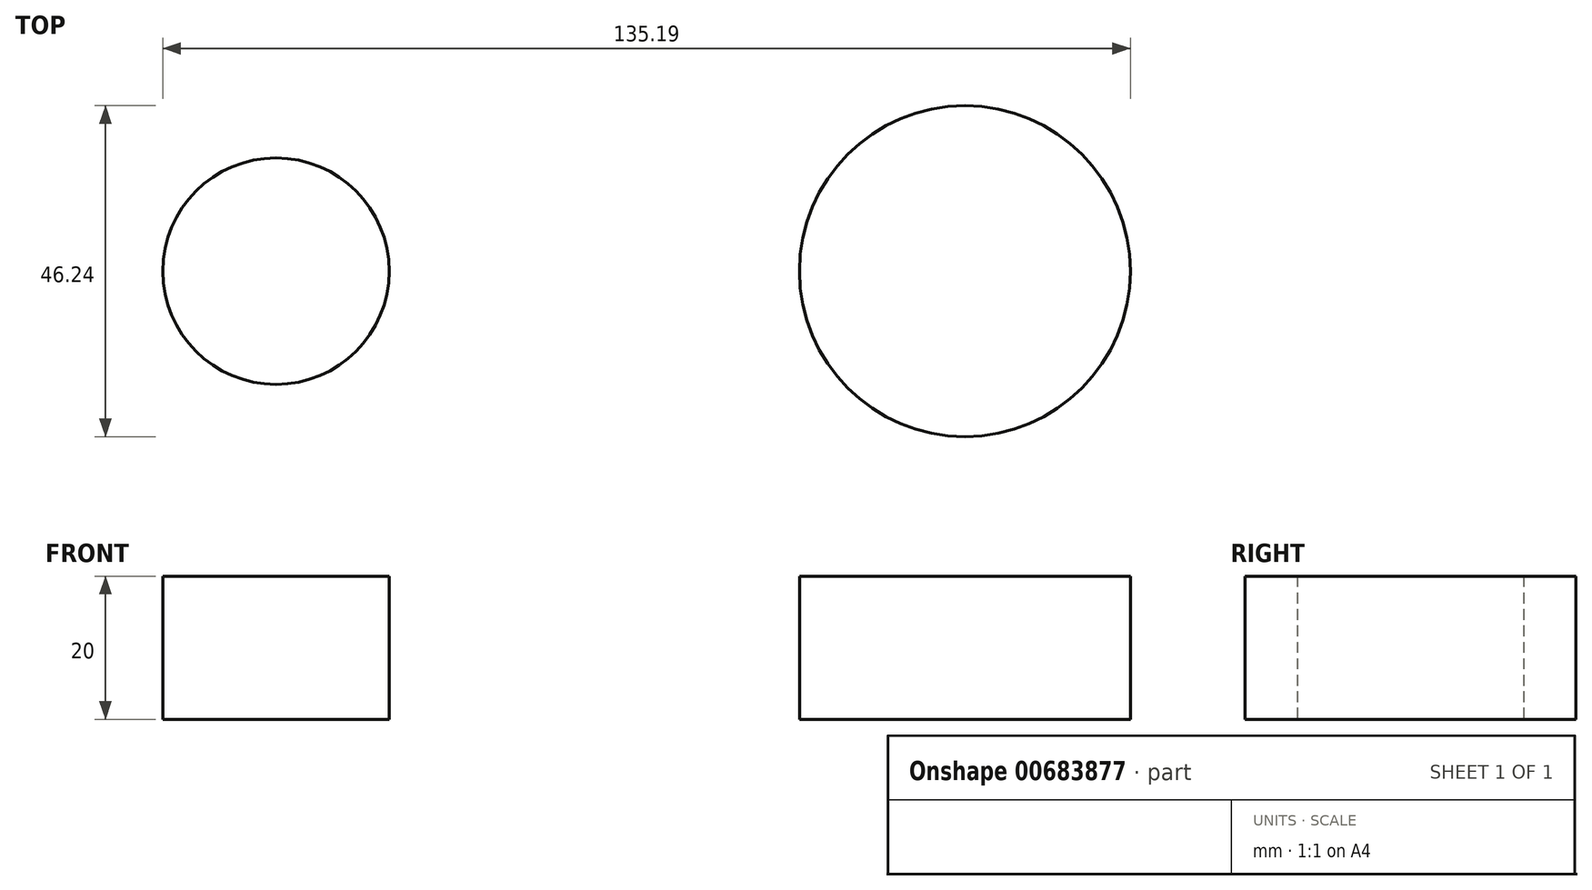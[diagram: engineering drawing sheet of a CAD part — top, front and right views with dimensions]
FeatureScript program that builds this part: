
annotation { "Feature Type Name" : "Feature", "Feature Type Description" : "" }
export const myFeature = defineFeature(function(context is Context, id is Id, definition is map)
    precondition{}
    {
        {
            var Q0;
            Q0=qCreatedBy(makeId("Top.planeOp"),FACE);
            var sketch = newSketch(context, id + "F0", { "sketchPlane" : qUnion([Q0])});
            skCircle(sketch, "E0", {"center": v(46.56, 0) * mm, "radius": 23.12 * mm});
            skSolve(sketch);
        }
        {
            var Q0;
            Q0=makeQuery(id+"F0.imprint","IMPRINT",FACE,{"disambiguationData":[TD([[makeQuery(id+"F0.imprint","IMPRINT",EDGE,{"derivedFrom":sQuery(id+"F0.wireOp",EDGE,"E0")}),1.0]])]});
            extrude(context, id + "F1", {"entities" : qUnion([Q0]), "depth" : 20 * mm, "offsetDistance" : 25 * mm});
        }
        {
            var Q0;
            Q0=qCreatedBy(makeId("Top.planeOp"),FACE);
            var sketch = newSketch(context, id + "F2", { "sketchPlane" : qUnion([Q0])});
            skCircle(sketch, "E1", {"center": v(-49.69, 0) * mm, "radius": 15.82 * mm});
            skSolve(sketch);
        }
        {
            var Q0;
            Q0=makeQuery(id+"F2.imprint","IMPRINT",FACE,{"disambiguationData":[TD([[makeQuery(id+"F2.imprint","IMPRINT",EDGE,{"derivedFrom":sQuery(id+"F2.wireOp",EDGE,"E1")}),1.0]])]});
            extrude(context, id + "F3", {"entities" : qUnion([Q0]), "depth" : 20 * mm, "offsetDistance" : 25 * mm});
        }
    });
